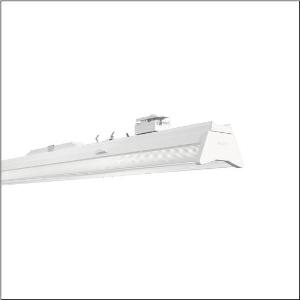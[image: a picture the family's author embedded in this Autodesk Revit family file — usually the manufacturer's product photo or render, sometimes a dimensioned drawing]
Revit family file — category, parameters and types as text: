
# Revit family: licross_r__21_performance_mo_51td16vnd8xg_f547
name_source: partatom
category: Lighting Fixtures
units: mm (PartAtom-declared; Revit-internal decimal feet)

## family parameters
Cut with Voids When Loaded = No
Host = Face
Light Source = No
Part Type = Normal
Room Calculation Point = No
Round Connector Dimension = Use Diameter
Shared = No

## types (1)
- --- (1 x LED, 8000 lm, 48.3 W, 4000K)
    Apparent Load = 48 VA
    CIE Flux Codes = 66 88 96 79 100
    Color Rendering = 90
    Color Temperature = 4000K
    Default Elevation = 1800 mm
    Description = Licross® 21 Performance MO, luminaire insert, of sheet steel, galvanised, coil coated, white, length: 1.500mm, width: 120mm, height: 123mm, LED rated luminous flux: 8.000lm, light colour: 940, SDCM (Standard Deviation of Colour Matching)MacAdam ≤ 2 SDCM (initial), control gear: DALI 2, CLO, with plug, 5-pole, with phase selection, mains connection: 220..240V, AC, 50/60Hz, start of lifetime: 48W, end of service life: 53W, internal wiring halogen-free, primary light control with lens, of plastic, primary optical cover: cover, of PMMA, light emission: direct/indirect distribution, primary light characteristic: symmetric, protection rating (complete): IP54, insulation class (complete): insulation class I (protective earthing), certification: CE, ENEC, VDE, UKCA, protection symbol: D if used in an environment with non-conductive dust loads with corresponding accessories, impact resistance: IK06, permissible ambient temperature for indoor applications: -25..+35°C, corresponds to IFS (International Featured Standards) requirements for safety and quality in the food industry, reducing of maximum allowable ambient temperature of 5°C with ceiling mounting, LABS conformity tested according to VDMA 24364:2018-05, packaging unit: 1 piece
    Height = 114 mm
    Lamp = 1 x LED
    Lamp Light Flux = 8000 lm
    Lamp Power = 48.3 W
    Lamp count = 1
    Length = 1500 mm
    Luminous efficacy = 166 lm/W
    Manufacturer = Siteco
    ModVariant = No
    Model = 51TD16VND8XG
    Mounting Place = Ceiling
    Mounting Type = Pendant
    Number of Poles = 1
    OnlyDefault = Yes
    Power Factor = 1
    Product Name = Licross® 21 Performance MO
    Product group = luminaire insert | ceiling pendant
    ProductGroupID = 901
    Protection Class = Protection class I
    Protection Degree = IP 54
    RLX_Detail_Level = 1
    RLX_Emergency_Light_Flux = 0 lm
    RLX_Emergency_Type = 0
    RLX_Emergency_Type_DB = No
    RlxData = <blob elided: 34277 chars, md5=461fd219>
    Socket = socket
    Standby Power = 0 W
    System Light Flux = 8000 lm
    System Power = 48 W
    Type Comments = factory setting: luminous flux: 100 % | dim-lin: 254 | 324 mA
    Type Image = l_1256138.jpg
    URL = http://relux.com
    VarID = @adj_095497
    Voltage = 0 V
    Weight = 0.00 kg
    Width = 120 mm

## geometry (parser evidence)
native form markers: Blend x4, Sweep x13
no freeform markers — native parametric forms only
